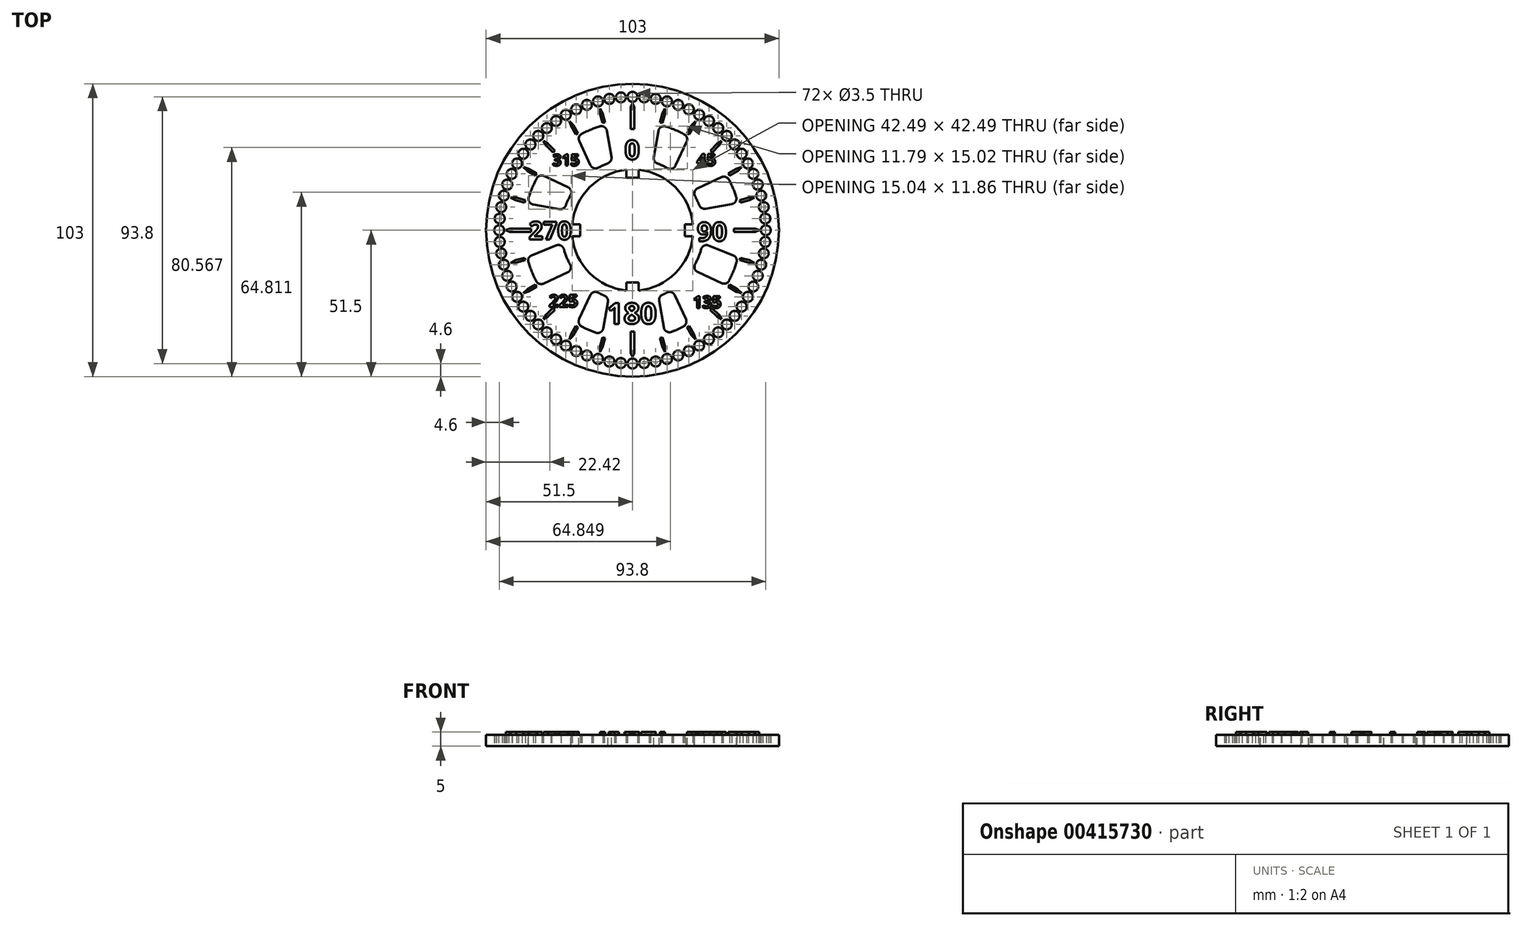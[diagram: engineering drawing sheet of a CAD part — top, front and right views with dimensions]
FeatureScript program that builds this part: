
annotation { "Feature Type Name" : "Feature", "Feature Type Description" : "" }
export const myFeature = defineFeature(function(context is Context, id is Id, definition is map)
    precondition{}
    {
        {
            var Q0;
            Q0=qCreatedBy(makeId("Top.planeOp"),FACE);
            var sketch = newSketch(context, id + "F0", { "sketchPlane" : qUnion([Q0])});
            skArc(sketch, "E0", {"start": v(-2.45, 20.86) * mm, "mid": v(-14.85, 14.85) * mm, "end": v(-20.86, 2.45) * mm});
            skLineSegment(sketch, "E1", {"start": v(0, 35.66) * mm, "end": v(0, -32.33) * mm, "construction": true});
            skLineSegment(sketch, "E2", {"start": v(-36.79, 0) * mm, "end": v(39.43, 0) * mm, "construction": true});
            skCircle(sketch, "E3", {"center": v(0, 0) * mm, "radius": 21.35 * mm});
            skLineSegment(sketch, "E4", {"start": v(0, 18.06) * mm, "end": v(-2.45, 18.06) * mm});
            skLineSegment(sketch, "E5", {"start": v(-2.45, 18.06) * mm, "end": v(-2.45, 20.86) * mm});
            skLineSegment(sketch, "E6.MirrorCS", {"start": v(0, 18.06) * mm, "end": v(2.45, 18.06) * mm});
            skLineSegment(sketch, "E7.MirrorCS", {"start": v(2.45, 18.06) * mm, "end": v(2.45, 20.86) * mm});
            skLineSegment(sketch, "E8.1.0", {"start": v(-18.06, -2.45) * mm, "end": v(-20.86, -2.45) * mm});
            skLineSegment(sketch, "E8.1.1", {"start": v(-18.06, 0) * mm, "end": v(-18.06, -2.45) * mm});
            skLineSegment(sketch, "E8.1.2", {"start": v(-18.06, 0) * mm, "end": v(-18.06, 2.45) * mm});
            skLineSegment(sketch, "E8.1.3", {"start": v(-18.06, 2.45) * mm, "end": v(-20.86, 2.45) * mm});
            skLineSegment(sketch, "E8.2.0", {"start": v(2.45, -18.06) * mm, "end": v(2.45, -20.86) * mm});
            skLineSegment(sketch, "E8.2.1", {"start": v(0, -18.06) * mm, "end": v(2.45, -18.06) * mm});
            skLineSegment(sketch, "E8.2.2", {"start": v(0, -18.06) * mm, "end": v(-2.45, -18.06) * mm});
            skLineSegment(sketch, "E8.2.3", {"start": v(-2.45, -18.06) * mm, "end": v(-2.45, -20.86) * mm});
            skLineSegment(sketch, "E8.3.0", {"start": v(18.06, 2.45) * mm, "end": v(20.86, 2.45) * mm});
            skLineSegment(sketch, "E8.3.1", {"start": v(18.06, 0) * mm, "end": v(18.06, 2.45) * mm});
            skLineSegment(sketch, "E8.3.2", {"start": v(18.06, 0) * mm, "end": v(18.06, -2.45) * mm});
            skLineSegment(sketch, "E8.3.3", {"start": v(18.06, -2.45) * mm, "end": v(20.86, -2.45) * mm});
            skArc(sketch, "E9.trimOffspring", {"start": v(20.86, 2.45) * mm, "mid": v(14.85, 14.85) * mm, "end": v(2.45, 20.86) * mm});
            skArc(sketch, "E10.trimOffspring", {"start": v(2.45, -20.86) * mm, "mid": v(14.85, -14.85) * mm, "end": v(20.86, -2.45) * mm});
            skArc(sketch, "E11.trimOffspring", {"start": v(-20.86, -2.45) * mm, "mid": v(-14.85, -14.85) * mm, "end": v(-2.45, -20.86) * mm});
            skCircle(sketch, "E12", {"center": v(0, 0) * mm, "radius": 24.63 * mm});
            skLineSegment(sketch, "E13", {"start": v(-1.6, 24.58) * mm, "end": v(-1.6, 48.9) * mm});
            skLineSegment(sketch, "E14", {"start": v(-1.6, 48.9) * mm, "end": v(1.67, 48.9) * mm});
            skLineSegment(sketch, "E15", {"start": v(1.67, 48.9) * mm, "end": v(1.67, 24.58) * mm});
            skCircle(sketch, "E16", {"center": v(0, 0) * mm, "radius": 21 * mm, "construction": true});
            skPoint(sketch, "E17", {"position": v(0, 21) * mm});
            skLineSegment(sketch, "E18", {"start": v(-7.13, 21) * mm, "end": v(7.07, 21) * mm, "construction": true});
            skPoint(sketch, "E19", {"position": v(0, 46.9) * mm});
            skLineSegment(sketch, "E20", {"start": v(-18.06, 46.9) * mm, "end": v(18.78, 46.9) * mm, "construction": true});
            skCircle(sketch, "E21", {"center": v(0, 46.9) * mm, "radius": 1.75 * mm});
            skLineSegment(sketch, "E22", {"start": v(-2.1, 21.25) * mm, "end": v(-2.1, 18.4) * mm});
            skLineSegment(sketch, "E23", {"start": v(-2.1, 18.4) * mm, "end": v(2.1, 18.4) * mm});
            skLineSegment(sketch, "E24", {"start": v(2.1, 18.4) * mm, "end": v(2.1, 21.25) * mm});
            skLineSegment(sketch, "E25.1.0", {"start": v(-21.25, -2.1) * mm, "end": v(-18.4, -2.1) * mm});
            skLineSegment(sketch, "E25.1.1", {"start": v(-18.4, -2.1) * mm, "end": v(-18.4, 2.1) * mm});
            skLineSegment(sketch, "E25.1.2", {"start": v(-18.4, 2.1) * mm, "end": v(-21.25, 2.1) * mm});
            skLineSegment(sketch, "E25.2.0", {"start": v(2.1, -21.25) * mm, "end": v(2.1, -18.4) * mm});
            skLineSegment(sketch, "E25.2.1", {"start": v(2.1, -18.4) * mm, "end": v(-2.1, -18.4) * mm});
            skLineSegment(sketch, "E25.2.2", {"start": v(-2.1, -18.4) * mm, "end": v(-2.1, -21.25) * mm});
            skLineSegment(sketch, "E25.3.0", {"start": v(21.25, 2.1) * mm, "end": v(18.4, 2.1) * mm});
            skLineSegment(sketch, "E25.3.1", {"start": v(18.4, 2.1) * mm, "end": v(18.4, -2.1) * mm});
            skLineSegment(sketch, "E25.3.2", {"start": v(18.4, -2.1) * mm, "end": v(21.25, -2.1) * mm});
            skCircle(sketch, "E26", {"center": v(0, 46.9) * mm, "radius": 4.35 * mm});
            skCircle(sketch, "E27", {"center": v(0, 0) * mm, "radius": 51.5 * mm});
            skCircle(sketch, "E28.1.0", {"center": v(-4.09, 46.72) * mm, "radius": 1.75 * mm});
            skCircle(sketch, "E28.2.0", {"center": v(-8.14, 46.19) * mm, "radius": 1.75 * mm});
            skCircle(sketch, "E28.3.0", {"center": v(-12.14, 45.3) * mm, "radius": 1.75 * mm});
            skCircle(sketch, "E28.4.0", {"center": v(-16.04, 44.07) * mm, "radius": 1.75 * mm});
            skCircle(sketch, "E28.5.0", {"center": v(-19.82, 42.5) * mm, "radius": 1.75 * mm});
            skCircle(sketch, "E28.6.0", {"center": v(-23.45, 40.62) * mm, "radius": 1.75 * mm});
            skCircle(sketch, "E28.7.0", {"center": v(-26.9, 38.42) * mm, "radius": 1.75 * mm});
            skCircle(sketch, "E28.8.0", {"center": v(-30.15, 35.93) * mm, "radius": 1.75 * mm});
            skCircle(sketch, "E28.9.0", {"center": v(-33.16, 33.16) * mm, "radius": 1.75 * mm});
            skCircle(sketch, "E28.10.0", {"center": v(-35.93, 30.15) * mm, "radius": 1.75 * mm});
            skCircle(sketch, "E28.11.0", {"center": v(-38.42, 26.9) * mm, "radius": 1.75 * mm});
            skCircle(sketch, "E28.12.0", {"center": v(-40.62, 23.45) * mm, "radius": 1.75 * mm});
            skCircle(sketch, "E28.13.0", {"center": v(-42.5, 19.82) * mm, "radius": 1.75 * mm});
            skCircle(sketch, "E28.14.0", {"center": v(-44.07, 16.04) * mm, "radius": 1.75 * mm});
            skCircle(sketch, "E28.15.0", {"center": v(-45.3, 12.14) * mm, "radius": 1.75 * mm});
            skCircle(sketch, "E28.16.0", {"center": v(-46.19, 8.14) * mm, "radius": 1.75 * mm});
            skCircle(sketch, "E28.17.0", {"center": v(-46.72, 4.09) * mm, "radius": 1.75 * mm});
            skCircle(sketch, "E28.18.0", {"center": v(-46.9, 0) * mm, "radius": 1.75 * mm});
            skCircle(sketch, "E28.19.0", {"center": v(-46.72, -4.09) * mm, "radius": 1.75 * mm});
            skCircle(sketch, "E28.20.0", {"center": v(-46.19, -8.14) * mm, "radius": 1.75 * mm});
            skCircle(sketch, "E28.21.0", {"center": v(-45.3, -12.14) * mm, "radius": 1.75 * mm});
            skCircle(sketch, "E28.22.0", {"center": v(-44.07, -16.04) * mm, "radius": 1.75 * mm});
            skCircle(sketch, "E28.23.0", {"center": v(-42.5, -19.82) * mm, "radius": 1.75 * mm});
            skCircle(sketch, "E28.24.0", {"center": v(-40.62, -23.45) * mm, "radius": 1.75 * mm});
            skCircle(sketch, "E28.25.0", {"center": v(-38.42, -26.9) * mm, "radius": 1.75 * mm});
            skCircle(sketch, "E28.26.0", {"center": v(-35.93, -30.15) * mm, "radius": 1.75 * mm});
            skCircle(sketch, "E28.27.0", {"center": v(-33.16, -33.16) * mm, "radius": 1.75 * mm});
            skCircle(sketch, "E28.28.0", {"center": v(-30.15, -35.93) * mm, "radius": 1.75 * mm});
            skCircle(sketch, "E28.29.0", {"center": v(-26.9, -38.42) * mm, "radius": 1.75 * mm});
            skCircle(sketch, "E28.30.0", {"center": v(-23.45, -40.62) * mm, "radius": 1.75 * mm});
            skCircle(sketch, "E28.31.0", {"center": v(-19.82, -42.5) * mm, "radius": 1.75 * mm});
            skCircle(sketch, "E28.32.0", {"center": v(-16.04, -44.07) * mm, "radius": 1.75 * mm});
            skCircle(sketch, "E28.33.0", {"center": v(-12.14, -45.3) * mm, "radius": 1.75 * mm});
            skCircle(sketch, "E28.34.0", {"center": v(-8.14, -46.19) * mm, "radius": 1.75 * mm});
            skCircle(sketch, "E28.35.0", {"center": v(-4.09, -46.72) * mm, "radius": 1.75 * mm});
            skCircle(sketch, "E28.36.0", {"center": v(0, -46.9) * mm, "radius": 1.75 * mm});
            skCircle(sketch, "E28.37.0", {"center": v(4.09, -46.72) * mm, "radius": 1.75 * mm});
            skCircle(sketch, "E28.38.0", {"center": v(8.14, -46.19) * mm, "radius": 1.75 * mm});
            skCircle(sketch, "E28.39.0", {"center": v(12.14, -45.3) * mm, "radius": 1.75 * mm});
            skCircle(sketch, "E28.40.0", {"center": v(16.04, -44.07) * mm, "radius": 1.75 * mm});
            skCircle(sketch, "E28.41.0", {"center": v(19.82, -42.5) * mm, "radius": 1.75 * mm});
            skCircle(sketch, "E28.42.0", {"center": v(23.45, -40.62) * mm, "radius": 1.75 * mm});
            skCircle(sketch, "E28.43.0", {"center": v(26.9, -38.42) * mm, "radius": 1.75 * mm});
            skCircle(sketch, "E28.44.0", {"center": v(30.15, -35.93) * mm, "radius": 1.75 * mm});
            skCircle(sketch, "E28.45.0", {"center": v(33.16, -33.16) * mm, "radius": 1.75 * mm});
            skCircle(sketch, "E28.46.0", {"center": v(35.93, -30.15) * mm, "radius": 1.75 * mm});
            skCircle(sketch, "E28.47.0", {"center": v(38.42, -26.9) * mm, "radius": 1.75 * mm});
            skCircle(sketch, "E28.48.0", {"center": v(40.62, -23.45) * mm, "radius": 1.75 * mm});
            skCircle(sketch, "E28.49.0", {"center": v(42.5, -19.82) * mm, "radius": 1.75 * mm});
            skCircle(sketch, "E28.50.0", {"center": v(44.07, -16.04) * mm, "radius": 1.75 * mm});
            skCircle(sketch, "E28.51.0", {"center": v(45.3, -12.14) * mm, "radius": 1.75 * mm});
            skCircle(sketch, "E28.52.0", {"center": v(46.19, -8.14) * mm, "radius": 1.75 * mm});
            skCircle(sketch, "E28.53.0", {"center": v(46.72, -4.09) * mm, "radius": 1.75 * mm});
            skCircle(sketch, "E28.54.0", {"center": v(46.9, 0) * mm, "radius": 1.75 * mm});
            skCircle(sketch, "E28.55.0", {"center": v(46.72, 4.09) * mm, "radius": 1.75 * mm});
            skCircle(sketch, "E28.56.0", {"center": v(46.19, 8.14) * mm, "radius": 1.75 * mm});
            skCircle(sketch, "E28.57.0", {"center": v(45.3, 12.14) * mm, "radius": 1.75 * mm});
            skCircle(sketch, "E28.58.0", {"center": v(44.07, 16.04) * mm, "radius": 1.75 * mm});
            skCircle(sketch, "E28.59.0", {"center": v(42.5, 19.82) * mm, "radius": 1.75 * mm});
            skCircle(sketch, "E28.60.0", {"center": v(40.62, 23.45) * mm, "radius": 1.75 * mm});
            skCircle(sketch, "E28.61.0", {"center": v(38.42, 26.9) * mm, "radius": 1.75 * mm});
            skCircle(sketch, "E28.62.0", {"center": v(35.93, 30.15) * mm, "radius": 1.75 * mm});
            skCircle(sketch, "E28.63.0", {"center": v(33.16, 33.16) * mm, "radius": 1.75 * mm});
            skCircle(sketch, "E28.64.0", {"center": v(30.15, 35.93) * mm, "radius": 1.75 * mm});
            skCircle(sketch, "E28.65.0", {"center": v(26.9, 38.42) * mm, "radius": 1.75 * mm});
            skCircle(sketch, "E28.66.0", {"center": v(23.45, 40.62) * mm, "radius": 1.75 * mm});
            skCircle(sketch, "E28.67.0", {"center": v(19.82, 42.5) * mm, "radius": 1.75 * mm});
            skCircle(sketch, "E28.68.0", {"center": v(16.04, 44.07) * mm, "radius": 1.75 * mm});
            skCircle(sketch, "E28.69.0", {"center": v(12.14, 45.3) * mm, "radius": 1.75 * mm});
            skCircle(sketch, "E28.70.0", {"center": v(8.14, 46.19) * mm, "radius": 1.75 * mm});
            skCircle(sketch, "E28.71.0", {"center": v(4.09, 46.72) * mm, "radius": 1.75 * mm});
            skCircle(sketch, "E29", {"center": v(0, 0) * mm, "radius": 42.33 * mm});
            skCircle(sketch, "E30", {"center": v(0, 0) * mm, "radius": 27.68 * mm});
            skSolve(sketch);
        }
        {
            var Q0;
            Q0=makeQuery(id+"F0.imprint","IMPRINT",FACE,{"disambiguationData":[TD([[makeQuery(id+"F0.imprint","IMPRINT",EDGE,{"derivedFrom":sQuery(id+"F0.wireOp",EDGE,"E27")}),1.0]])]});
            var Q1;
            {var subQ16=sQuery(id+"F0.wireOp",EDGE,"E14");Q1=makeQuery(id+"F0.imprint","IMPRINT",FACE,{"disambiguationData":[TD([[makeQuery(id+"F0.imprint","IMPRINT",EDGE,{"derivedFrom":subQ16}),1.0]])]});}
            var Q2;
            {var subQ0=sQuery(id+"F0.wireOp",EDGE,"E26");var subQ1=sQuery(id+"F0.wireOp",EDGE,"E13");var subQ2=makeQuery(id+"F0.imprint","INTERSECT",VERTEX,{"derivedFrom":[subQ1,subQ0]});Q2=makeQuery(id+"F0.imprint","IMPRINT",FACE,{"disambiguationData":[TD([[makeQuery(id+"F0.imprint","IMPRINT",EDGE,{"disambiguationData":[TD([[subQ2,-1.0]])],"derivedFrom":subQ1}),-1.0]])]});}
            var Q3;
            {var subQ0=sQuery(id+"F0.wireOp",EDGE,"E14");Q3=makeQuery(id+"F0.imprint","IMPRINT",FACE,{"disambiguationData":[TD([[makeQuery(id+"F0.imprint","IMPRINT",EDGE,{"derivedFrom":subQ0}),-1.0]])]});}
            var Q4;
            {var subQ0=sQuery(id+"F0.wireOp",EDGE,"E13");var subQ1=sQuery(id+"F0.wireOp",EDGE,"E12");var subQ2=makeQuery(id+"F0.imprint","INTERSECT",VERTEX,{"derivedFrom":[subQ1,subQ0]});Q4=makeQuery(id+"F0.imprint","IMPRINT",FACE,{"disambiguationData":[TD([[makeQuery(id+"F0.imprint","IMPRINT",EDGE,{"disambiguationData":[TD([[subQ2,1.0]])],"derivedFrom":subQ1}),-1.0]])]});}
            var Q5;
            {var subQ0=sQuery(id+"F0.wireOp",EDGE,"E3");var subQ4=makeQuery(id+"F0.imprint","INTERSECT",VERTEX,{"derivedFrom":[subQ0,sQuery(id+"F0.wireOp",EDGE,"E24")]});Q5=makeQuery(id+"F0.imprint","IMPRINT",FACE,{"disambiguationData":[TD([[makeQuery(id+"F0.imprint","IMPRINT",EDGE,{"disambiguationData":[TD([[subQ4,1.0]])],"derivedFrom":subQ0}),-1.0]])]});}
            var Q6;
            {var subQ5=sQuery(id+"F0.wireOp",EDGE,"E25.1.1");Q6=makeQuery(id+"F0.imprint","IMPRINT",FACE,{"disambiguationData":[TD([[makeQuery(id+"F0.imprint","IMPRINT",EDGE,{"derivedFrom":subQ5}),1.0]])]});}
            var Q7;
            {var subQ0=sQuery(id+"F0.wireOp",EDGE,"E22");Q7=makeQuery(id+"F0.imprint","IMPRINT",FACE,{"disambiguationData":[TD([[makeQuery(id+"F0.imprint","IMPRINT",EDGE,{"derivedFrom":subQ0}),1.0]])]});}
            var Q8;
            {var subQ5=sQuery(id+"F0.wireOp",EDGE,"E25.3.1");Q8=makeQuery(id+"F0.imprint","IMPRINT",FACE,{"disambiguationData":[TD([[makeQuery(id+"F0.imprint","IMPRINT",EDGE,{"derivedFrom":subQ5}),1.0]])]});}
            var Q9;
            {var subQ5=sQuery(id+"F0.wireOp",EDGE,"E25.2.1");Q9=makeQuery(id+"F0.imprint","IMPRINT",FACE,{"disambiguationData":[TD([[makeQuery(id+"F0.imprint","IMPRINT",EDGE,{"derivedFrom":subQ5}),1.0]])]});}
            var Q10;
            {var subQ0=sQuery(id+"F0.wireOp",EDGE,"E30");var subQ1=sQuery(id+"F0.wireOp",EDGE,"E13");var subQ2=makeQuery(id+"F0.imprint","INTERSECT",VERTEX,{"derivedFrom":[subQ1,subQ0]});Q10=makeQuery(id+"F0.imprint","IMPRINT",FACE,{"disambiguationData":[TD([[makeQuery(id+"F0.imprint","IMPRINT",EDGE,{"disambiguationData":[TD([[subQ2,-1.0]])],"derivedFrom":subQ1}),1.0]])]});}
            var Q11;
            {var subQ0=sQuery(id+"F0.wireOp",EDGE,"E13");var subQ1=sQuery(id+"F0.wireOp",EDGE,"E12");var subQ2=makeQuery(id+"F0.imprint","INTERSECT",VERTEX,{"derivedFrom":[subQ1,subQ0]});Q11=makeQuery(id+"F0.imprint","IMPRINT",FACE,{"disambiguationData":[TD([[makeQuery(id+"F0.imprint","IMPRINT",EDGE,{"disambiguationData":[TD([[subQ2,-1.0]])],"derivedFrom":subQ1}),-1.0]])]});}
            var Q12;
            {var subQ0=sQuery(id+"F0.wireOp",EDGE,"E30");var subQ1=sQuery(id+"F0.wireOp",EDGE,"E13");var subQ2=makeQuery(id+"F0.imprint","INTERSECT",VERTEX,{"derivedFrom":[subQ1,subQ0]});Q12=makeQuery(id+"F0.imprint","IMPRINT",FACE,{"disambiguationData":[TD([[makeQuery(id+"F0.imprint","IMPRINT",EDGE,{"disambiguationData":[TD([[subQ2,-1.0]])],"derivedFrom":subQ1}),-1.0]])]});}
            var Q13;
            {var subQ0=sQuery(id+"F0.wireOp",EDGE,"E29");var subQ1=sQuery(id+"F0.wireOp",EDGE,"E13");var subQ2=makeQuery(id+"F0.imprint","INTERSECT",VERTEX,{"derivedFrom":[subQ1,subQ0]});Q13=makeQuery(id+"F0.imprint","IMPRINT",FACE,{"disambiguationData":[TD([[makeQuery(id+"F0.imprint","IMPRINT",EDGE,{"disambiguationData":[TD([[subQ2,-1.0]])],"derivedFrom":subQ1}),-1.0]])]});}
            extrude(context, id + "F1", {"entities" : qUnion([Q0, Q1, Q2, Q3, Q4, Q5, Q6, Q7, Q8, Q9, Q10, Q11, Q12, Q13]), "depth" : 4 * mm});
        }
        {
            var Q0;
            Q0=makeQuery(id+"F1.opExtrude","CAP_FACE",FACE,{"disambiguationData":[OSD([sQuery(id+"F0.wireOp",EDGE,"E3"),sQuery(id+"F0.wireOp",EDGE,"E21"),sQuery(id+"F0.wireOp",EDGE,"E22"),sQuery(id+"F0.wireOp",EDGE,"E23"),sQuery(id+"F0.wireOp",EDGE,"E24"),sQuery(id+"F0.wireOp",EDGE,"E25.1.0"),sQuery(id+"F0.wireOp",EDGE,"E25.1.1"),sQuery(id+"F0.wireOp",EDGE,"E25.1.2"),sQuery(id+"F0.wireOp",EDGE,"E25.2.0"),sQuery(id+"F0.wireOp",EDGE,"E25.2.1"),sQuery(id+"F0.wireOp",EDGE,"E25.2.2"),sQuery(id+"F0.wireOp",EDGE,"E25.3.0"),sQuery(id+"F0.wireOp",EDGE,"E25.3.1"),sQuery(id+"F0.wireOp",EDGE,"E25.3.2"),sQuery(id+"F0.wireOp",EDGE,"E27"),sQuery(id+"F0.wireOp",EDGE,"E28.1.0"),sQuery(id+"F0.wireOp",EDGE,"E28.2.0"),sQuery(id+"F0.wireOp",EDGE,"E28.3.0"),sQuery(id+"F0.wireOp",EDGE,"E28.4.0"),sQuery(id+"F0.wireOp",EDGE,"E28.5.0"),sQuery(id+"F0.wireOp",EDGE,"E28.6.0"),sQuery(id+"F0.wireOp",EDGE,"E28.7.0"),sQuery(id+"F0.wireOp",EDGE,"E28.8.0"),sQuery(id+"F0.wireOp",EDGE,"E28.9.0"),sQuery(id+"F0.wireOp",EDGE,"E28.10.0"),sQuery(id+"F0.wireOp",EDGE,"E28.11.0"),sQuery(id+"F0.wireOp",EDGE,"E28.12.0"),sQuery(id+"F0.wireOp",EDGE,"E28.13.0"),sQuery(id+"F0.wireOp",EDGE,"E28.14.0"),sQuery(id+"F0.wireOp",EDGE,"E28.15.0"),sQuery(id+"F0.wireOp",EDGE,"E28.16.0"),sQuery(id+"F0.wireOp",EDGE,"E28.17.0"),sQuery(id+"F0.wireOp",EDGE,"E28.18.0"),sQuery(id+"F0.wireOp",EDGE,"E28.19.0"),sQuery(id+"F0.wireOp",EDGE,"E28.20.0"),sQuery(id+"F0.wireOp",EDGE,"E28.21.0"),sQuery(id+"F0.wireOp",EDGE,"E28.22.0"),sQuery(id+"F0.wireOp",EDGE,"E28.23.0"),sQuery(id+"F0.wireOp",EDGE,"E28.24.0"),sQuery(id+"F0.wireOp",EDGE,"E28.25.0"),sQuery(id+"F0.wireOp",EDGE,"E28.26.0"),sQuery(id+"F0.wireOp",EDGE,"E28.27.0"),sQuery(id+"F0.wireOp",EDGE,"E28.28.0"),sQuery(id+"F0.wireOp",EDGE,"E28.29.0"),sQuery(id+"F0.wireOp",EDGE,"E28.30.0"),sQuery(id+"F0.wireOp",EDGE,"E28.31.0"),sQuery(id+"F0.wireOp",EDGE,"E28.32.0"),sQuery(id+"F0.wireOp",EDGE,"E28.33.0"),sQuery(id+"F0.wireOp",EDGE,"E28.34.0"),sQuery(id+"F0.wireOp",EDGE,"E28.35.0"),sQuery(id+"F0.wireOp",EDGE,"E28.36.0"),sQuery(id+"F0.wireOp",EDGE,"E28.37.0"),sQuery(id+"F0.wireOp",EDGE,"E28.38.0"),sQuery(id+"F0.wireOp",EDGE,"E28.39.0"),sQuery(id+"F0.wireOp",EDGE,"E28.40.0"),sQuery(id+"F0.wireOp",EDGE,"E28.41.0"),sQuery(id+"F0.wireOp",EDGE,"E28.42.0"),sQuery(id+"F0.wireOp",EDGE,"E28.43.0"),sQuery(id+"F0.wireOp",EDGE,"E28.44.0"),sQuery(id+"F0.wireOp",EDGE,"E28.45.0"),sQuery(id+"F0.wireOp",EDGE,"E28.46.0"),sQuery(id+"F0.wireOp",EDGE,"E28.47.0"),sQuery(id+"F0.wireOp",EDGE,"E28.48.0"),sQuery(id+"F0.wireOp",EDGE,"E28.49.0"),sQuery(id+"F0.wireOp",EDGE,"E28.50.0"),sQuery(id+"F0.wireOp",EDGE,"E28.51.0"),sQuery(id+"F0.wireOp",EDGE,"E28.52.0"),sQuery(id+"F0.wireOp",EDGE,"E28.53.0"),sQuery(id+"F0.wireOp",EDGE,"E28.54.0"),sQuery(id+"F0.wireOp",EDGE,"E28.55.0"),sQuery(id+"F0.wireOp",EDGE,"E28.56.0"),sQuery(id+"F0.wireOp",EDGE,"E28.57.0"),sQuery(id+"F0.wireOp",EDGE,"E28.58.0"),sQuery(id+"F0.wireOp",EDGE,"E28.59.0"),sQuery(id+"F0.wireOp",EDGE,"E28.60.0"),sQuery(id+"F0.wireOp",EDGE,"E28.61.0"),sQuery(id+"F0.wireOp",EDGE,"E28.62.0"),sQuery(id+"F0.wireOp",EDGE,"E28.63.0"),sQuery(id+"F0.wireOp",EDGE,"E28.64.0"),sQuery(id+"F0.wireOp",EDGE,"E28.65.0"),sQuery(id+"F0.wireOp",EDGE,"E28.66.0"),sQuery(id+"F0.wireOp",EDGE,"E28.67.0"),sQuery(id+"F0.wireOp",EDGE,"E28.68.0"),sQuery(id+"F0.wireOp",EDGE,"E28.69.0"),sQuery(id+"F0.wireOp",EDGE,"E28.70.0"),sQuery(id+"F0.wireOp",EDGE,"E28.71.0")])],"isStart":false});
            var sketch = newSketch(context, id + "F2", { "sketchPlane" : qUnion([Q0])});
            skCircle(sketch, "E31", {"center": v(0, 0) * mm, "radius": 42.4 * mm});
            skCircle(sketch, "E32", {"center": v(0, 0) * mm, "radius": 25.92 * mm});
            skSolve(sketch);
        }
        {
            var Q0;
            Q0=makeQuery(id+"F1.opExtrude","CAP_FACE",FACE,{"disambiguationData":[OSD([sQuery(id+"F0.wireOp",EDGE,"E3"),sQuery(id+"F0.wireOp",EDGE,"E21"),sQuery(id+"F0.wireOp",EDGE,"E22"),sQuery(id+"F0.wireOp",EDGE,"E23"),sQuery(id+"F0.wireOp",EDGE,"E24"),sQuery(id+"F0.wireOp",EDGE,"E25.1.0"),sQuery(id+"F0.wireOp",EDGE,"E25.1.1"),sQuery(id+"F0.wireOp",EDGE,"E25.1.2"),sQuery(id+"F0.wireOp",EDGE,"E25.2.0"),sQuery(id+"F0.wireOp",EDGE,"E25.2.1"),sQuery(id+"F0.wireOp",EDGE,"E25.2.2"),sQuery(id+"F0.wireOp",EDGE,"E25.3.0"),sQuery(id+"F0.wireOp",EDGE,"E25.3.1"),sQuery(id+"F0.wireOp",EDGE,"E25.3.2"),sQuery(id+"F0.wireOp",EDGE,"E27"),sQuery(id+"F0.wireOp",EDGE,"E28.1.0"),sQuery(id+"F0.wireOp",EDGE,"E28.2.0"),sQuery(id+"F0.wireOp",EDGE,"E28.3.0"),sQuery(id+"F0.wireOp",EDGE,"E28.4.0"),sQuery(id+"F0.wireOp",EDGE,"E28.5.0"),sQuery(id+"F0.wireOp",EDGE,"E28.6.0"),sQuery(id+"F0.wireOp",EDGE,"E28.7.0"),sQuery(id+"F0.wireOp",EDGE,"E28.8.0"),sQuery(id+"F0.wireOp",EDGE,"E28.9.0"),sQuery(id+"F0.wireOp",EDGE,"E28.10.0"),sQuery(id+"F0.wireOp",EDGE,"E28.11.0"),sQuery(id+"F0.wireOp",EDGE,"E28.12.0"),sQuery(id+"F0.wireOp",EDGE,"E28.13.0"),sQuery(id+"F0.wireOp",EDGE,"E28.14.0"),sQuery(id+"F0.wireOp",EDGE,"E28.15.0"),sQuery(id+"F0.wireOp",EDGE,"E28.16.0"),sQuery(id+"F0.wireOp",EDGE,"E28.17.0"),sQuery(id+"F0.wireOp",EDGE,"E28.18.0"),sQuery(id+"F0.wireOp",EDGE,"E28.19.0"),sQuery(id+"F0.wireOp",EDGE,"E28.20.0"),sQuery(id+"F0.wireOp",EDGE,"E28.21.0"),sQuery(id+"F0.wireOp",EDGE,"E28.22.0"),sQuery(id+"F0.wireOp",EDGE,"E28.23.0"),sQuery(id+"F0.wireOp",EDGE,"E28.24.0"),sQuery(id+"F0.wireOp",EDGE,"E28.25.0"),sQuery(id+"F0.wireOp",EDGE,"E28.26.0"),sQuery(id+"F0.wireOp",EDGE,"E28.27.0"),sQuery(id+"F0.wireOp",EDGE,"E28.28.0"),sQuery(id+"F0.wireOp",EDGE,"E28.29.0"),sQuery(id+"F0.wireOp",EDGE,"E28.30.0"),sQuery(id+"F0.wireOp",EDGE,"E28.31.0"),sQuery(id+"F0.wireOp",EDGE,"E28.32.0"),sQuery(id+"F0.wireOp",EDGE,"E28.33.0"),sQuery(id+"F0.wireOp",EDGE,"E28.34.0"),sQuery(id+"F0.wireOp",EDGE,"E28.35.0"),sQuery(id+"F0.wireOp",EDGE,"E28.36.0"),sQuery(id+"F0.wireOp",EDGE,"E28.37.0"),sQuery(id+"F0.wireOp",EDGE,"E28.38.0"),sQuery(id+"F0.wireOp",EDGE,"E28.39.0"),sQuery(id+"F0.wireOp",EDGE,"E28.40.0"),sQuery(id+"F0.wireOp",EDGE,"E28.41.0"),sQuery(id+"F0.wireOp",EDGE,"E28.42.0"),sQuery(id+"F0.wireOp",EDGE,"E28.43.0"),sQuery(id+"F0.wireOp",EDGE,"E28.44.0"),sQuery(id+"F0.wireOp",EDGE,"E28.45.0"),sQuery(id+"F0.wireOp",EDGE,"E28.46.0"),sQuery(id+"F0.wireOp",EDGE,"E28.47.0"),sQuery(id+"F0.wireOp",EDGE,"E28.48.0"),sQuery(id+"F0.wireOp",EDGE,"E28.49.0"),sQuery(id+"F0.wireOp",EDGE,"E28.50.0"),sQuery(id+"F0.wireOp",EDGE,"E28.51.0"),sQuery(id+"F0.wireOp",EDGE,"E28.52.0"),sQuery(id+"F0.wireOp",EDGE,"E28.53.0"),sQuery(id+"F0.wireOp",EDGE,"E28.54.0"),sQuery(id+"F0.wireOp",EDGE,"E28.55.0"),sQuery(id+"F0.wireOp",EDGE,"E28.56.0"),sQuery(id+"F0.wireOp",EDGE,"E28.57.0"),sQuery(id+"F0.wireOp",EDGE,"E28.58.0"),sQuery(id+"F0.wireOp",EDGE,"E28.59.0"),sQuery(id+"F0.wireOp",EDGE,"E28.60.0"),sQuery(id+"F0.wireOp",EDGE,"E28.61.0"),sQuery(id+"F0.wireOp",EDGE,"E28.62.0"),sQuery(id+"F0.wireOp",EDGE,"E28.63.0"),sQuery(id+"F0.wireOp",EDGE,"E28.64.0"),sQuery(id+"F0.wireOp",EDGE,"E28.65.0"),sQuery(id+"F0.wireOp",EDGE,"E28.66.0"),sQuery(id+"F0.wireOp",EDGE,"E28.67.0"),sQuery(id+"F0.wireOp",EDGE,"E28.68.0"),sQuery(id+"F0.wireOp",EDGE,"E28.69.0"),sQuery(id+"F0.wireOp",EDGE,"E28.70.0"),sQuery(id+"F0.wireOp",EDGE,"E28.71.0")])],"isStart":false});
            var sketch = newSketch(context, id + "F3", { "sketchPlane" : qUnion([Q0])});
            skLineSegment(sketch, "E33", {"start": v(0, 43.22) * mm, "end": v(-0.58, 43.22) * mm});
            skLineSegment(sketch, "E34", {"start": v(-0.58, 43.22) * mm, "end": v(-0.58, 35.64) * mm});
            skLineSegment(sketch, "E35", {"start": v(-0.58, 35.64) * mm, "end": v(0, 35.64) * mm});
            skLineSegment(sketch, "E36", {"start": v(0, 44.58) * mm, "end": v(0, 29) * mm, "construction": true});
            skLineSegment(sketch, "E37.MirrorCS", {"start": v(0, 43.22) * mm, "end": v(0.58, 43.22) * mm});
            skLineSegment(sketch, "E38.MirrorCS", {"start": v(0.58, 43.22) * mm, "end": v(0.58, 35.64) * mm});
            skLineSegment(sketch, "E39.MirrorCS", {"start": v(0.58, 35.64) * mm, "end": v(0, 35.64) * mm});
            skLineSegment(sketch, "E40", {"start": v(-0.58, 43.22) * mm, "end": v(0, 44.58) * mm});
            skLineSegment(sketch, "E41", {"start": v(0.58, 43.22) * mm, "end": v(0, 44.58) * mm});
            skText(sketch, "E42", { "text": "0", "fontName": "OpenSans-Bold.ttf"});
            skLineSegment(sketch, "E43.1.0", {"start": v(-43.22, -0.58) * mm, "end": v(-44.58, 0) * mm});
            skLineSegment(sketch, "E43.1.1", {"start": v(-43.22, 0.58) * mm, "end": v(-44.58, 0) * mm});
            skLineSegment(sketch, "E43.1.2", {"start": v(-43.22, 0.58) * mm, "end": v(-35.64, 0.58) * mm});
            skLineSegment(sketch, "E43.1.3", {"start": v(-35.64, 0.58) * mm, "end": v(-35.64, 0) * mm});
            skLineSegment(sketch, "E43.1.4", {"start": v(-35.64, -0.58) * mm, "end": v(-35.64, 0) * mm});
            skLineSegment(sketch, "E43.1.5", {"start": v(-43.22, -0.58) * mm, "end": v(-35.64, -0.58) * mm});
            skLineSegment(sketch, "E43.2.0", {"start": v(0.58, -43.22) * mm, "end": v(0, -44.58) * mm});
            skLineSegment(sketch, "E43.2.1", {"start": v(-0.58, -43.22) * mm, "end": v(0, -44.58) * mm});
            skLineSegment(sketch, "E43.2.2", {"start": v(-0.58, -43.22) * mm, "end": v(-0.58, -35.64) * mm});
            skLineSegment(sketch, "E43.2.3", {"start": v(-0.58, -35.64) * mm, "end": v(0, -35.64) * mm});
            skLineSegment(sketch, "E43.2.4", {"start": v(0.58, -35.64) * mm, "end": v(0, -35.64) * mm});
            skLineSegment(sketch, "E43.2.5", {"start": v(0.58, -43.22) * mm, "end": v(0.58, -35.64) * mm});
            skLineSegment(sketch, "E43.3.0", {"start": v(43.22, 0.58) * mm, "end": v(44.58, 0) * mm});
            skLineSegment(sketch, "E43.3.1", {"start": v(43.22, -0.58) * mm, "end": v(44.58, 0) * mm});
            skLineSegment(sketch, "E43.3.2", {"start": v(43.22, -0.58) * mm, "end": v(35.64, -0.58) * mm});
            skLineSegment(sketch, "E43.3.3", {"start": v(35.64, -0.58) * mm, "end": v(35.64, 0) * mm});
            skLineSegment(sketch, "E43.3.4", {"start": v(35.64, 0.58) * mm, "end": v(35.64, 0) * mm});
            skLineSegment(sketch, "E43.3.5", {"start": v(43.22, 0.58) * mm, "end": v(35.64, 0.58) * mm});
            skPoint(sketch, "E43.center", {"position": v(0, 0) * mm});
            skText(sketch, "E44", { "text": "90", "fontName": "OpenSans-Bold.ttf"});
            skText(sketch, "E45", { "text": "180", "fontName": "OpenSans-Bold.ttf"});
            skPoint(sketch, "E46", {"position": v(0, 36.8) * mm});
            skText(sketch, "E47", { "text": "270", "fontName": "OpenSans-Bold.ttf"});
            const initialGuessF3  = {"E42": [-0.00281, 0.02492, 1, 0, 0.00675], "E44": [0.0227, -0.0038, 1, 0, 0.00662], "E45": [-0.00899, -0.03293, 1, 0, 0.00736], "E47": [-0.03652, -0.00328, 1, 0, 0.00634]};
            skSetInitialGuess(sketch, initialGuessF3);
            skSolve(sketch);
        }
        {
            var Q0;
            Q0 = qSketchRegion(id + "F3", true);
            extrude(context, id + "F4", {"entities" : qUnion([Q0]), "operationType" : NewBodyOperationType.ADD, "depth" : 1 * mm});
        }
        {
            var Q0;
            {var subQ0=sQuery(id+"F0.wireOp",EDGE,"E28.27.0");var subQ1=sQuery(id+"F0.wireOp",EDGE,"E28.26.0");var subQ2=sQuery(id+"F0.wireOp",EDGE,"E28.25.0");var subQ3=sQuery(id+"F0.wireOp",EDGE,"E28.46.0");var subQ4=sQuery(id+"F0.wireOp",EDGE,"E28.24.0");var subQ5=sQuery(id+"F0.wireOp",EDGE,"E28.45.0");var subQ6=sQuery(id+"F0.wireOp",EDGE,"E28.23.0");var subQ7=sQuery(id+"F0.wireOp",EDGE,"E28.44.0");var subQ8=sQuery(id+"F0.wireOp",EDGE,"E28.22.0");var subQ9=sQuery(id+"F0.wireOp",EDGE,"E28.43.0");var subQ10=sQuery(id+"F0.wireOp",EDGE,"E28.21.0");var subQ11=sQuery(id+"F0.wireOp",EDGE,"E28.42.0");var subQ12=sQuery(id+"F0.wireOp",EDGE,"E28.20.0");var subQ13=sQuery(id+"F0.wireOp",EDGE,"E28.41.0");var subQ14=sQuery(id+"F0.wireOp",EDGE,"E28.19.0");var subQ15=sQuery(id+"F0.wireOp",EDGE,"E28.17.0");var subQ16=sQuery(id+"F0.wireOp",EDGE,"E28.16.0");var subQ17=sQuery(id+"F0.wireOp",EDGE,"E28.10.0");var subQ18=sQuery(id+"F0.wireOp",EDGE,"E28.9.0");var subQ19=sQuery(id+"F0.wireOp",EDGE,"E28.18.0");var subQ20=sQuery(id+"F0.wireOp",EDGE,"E28.40.0");var subQ21=sQuery(id+"F0.wireOp",EDGE,"E28.7.0");var subQ22=sQuery(id+"F0.wireOp",EDGE,"E28.6.0");var subQ23=sQuery(id+"F0.wireOp",EDGE,"E28.15.0");var subQ24=sQuery(id+"F0.wireOp",EDGE,"E28.37.0");var subQ25=sQuery(id+"F0.wireOp",EDGE,"E28.5.0");var subQ26=sQuery(id+"F0.wireOp",EDGE,"E28.14.0");var subQ27=sQuery(id+"F0.wireOp",EDGE,"E28.36.0");var subQ28=sQuery(id+"F0.wireOp",EDGE,"E25.1.0");var subQ29=sQuery(id+"F0.wireOp",EDGE,"E24");var subQ30=sQuery(id+"F0.wireOp",EDGE,"E23");var subQ31=sQuery(id+"F0.wireOp",EDGE,"E22");var subQ32=sQuery(id+"F0.wireOp",EDGE,"E21");var subQ33=sQuery(id+"F0.wireOp",EDGE,"E25.1.1");var subQ34=sQuery(id+"F0.wireOp",EDGE,"E28.28.0");var subQ35=sQuery(id+"F0.wireOp",EDGE,"E3");var subQ36=sQuery(id+"F0.wireOp",EDGE,"E25.3.0");var subQ37=sQuery(id+"F0.wireOp",EDGE,"E28.4.0");var subQ38=sQuery(id+"F0.wireOp",EDGE,"E28.13.0");var subQ39=sQuery(id+"F0.wireOp",EDGE,"E28.35.0");var subQ40=sQuery(id+"F0.wireOp",EDGE,"E25.2.0");var subQ41=sQuery(id+"F0.wireOp",EDGE,"E25.3.2");var subQ42=sQuery(id+"F0.wireOp",EDGE,"E25.1.2");var subQ43=sQuery(id+"F0.wireOp",EDGE,"E25.2.2");var subQ44=sQuery(id+"F0.wireOp",EDGE,"E25.2.1");var subQ45=sQuery(id+"F0.wireOp",EDGE,"E25.3.1");var subQ46=sQuery(id+"F0.wireOp",EDGE,"E28.8.0");var subQ47=sQuery(id+"F0.wireOp",EDGE,"E28.30.0");var subQ48=sQuery(id+"F0.wireOp",EDGE,"E27");var subQ49=sQuery(id+"F0.wireOp",EDGE,"E28.1.0");var subQ50=sQuery(id+"F0.wireOp",EDGE,"E28.2.0");var subQ51=sQuery(id+"F0.wireOp",EDGE,"E28.11.0");var subQ52=sQuery(id+"F0.wireOp",EDGE,"E28.33.0");var subQ53=sQuery(id+"F0.wireOp",EDGE,"E28.3.0");var subQ54=sQuery(id+"F0.wireOp",EDGE,"E28.12.0");var subQ55=sQuery(id+"F0.wireOp",EDGE,"E28.34.0");var subQ56=sQuery(id+"F0.wireOp",EDGE,"E28.29.0");var subQ57=sQuery(id+"F0.wireOp",EDGE,"E28.31.0");var subQ58=sQuery(id+"F0.wireOp",EDGE,"E28.32.0");var subQ59=sQuery(id+"F0.wireOp",EDGE,"E28.55.0");var subQ60=sQuery(id+"F0.wireOp",EDGE,"E28.58.0");var subQ61=sQuery(id+"F0.wireOp",EDGE,"E28.59.0");var subQ62=sQuery(id+"F0.wireOp",EDGE,"E28.60.0");var subQ63=sQuery(id+"F0.wireOp",EDGE,"E28.38.0");var subQ64=sQuery(id+"F0.wireOp",EDGE,"E28.61.0");var subQ65=sQuery(id+"F0.wireOp",EDGE,"E28.39.0");var subQ66=sQuery(id+"F0.wireOp",EDGE,"E28.62.0");var subQ67=sQuery(id+"F0.wireOp",EDGE,"E28.65.0");var subQ68=sQuery(id+"F0.wireOp",EDGE,"E28.66.0");var subQ69=sQuery(id+"F0.wireOp",EDGE,"E28.67.0");var subQ70=sQuery(id+"F0.wireOp",EDGE,"E28.68.0");var subQ71=sQuery(id+"F0.wireOp",EDGE,"E28.69.0");var subQ72=sQuery(id+"F0.wireOp",EDGE,"E28.47.0");var subQ73=sQuery(id+"F0.wireOp",EDGE,"E28.48.0");var subQ74=sQuery(id+"F0.wireOp",EDGE,"E28.49.0");var subQ75=sQuery(id+"F0.wireOp",EDGE,"E28.50.0");var subQ76=sQuery(id+"F0.wireOp",EDGE,"E28.51.0");var subQ77=sQuery(id+"F0.wireOp",EDGE,"E28.52.0");var subQ78=sQuery(id+"F0.wireOp",EDGE,"E28.53.0");var subQ79=sQuery(id+"F0.wireOp",EDGE,"E28.54.0");var subQ80=sQuery(id+"F0.wireOp",EDGE,"E28.56.0");var subQ81=sQuery(id+"F0.wireOp",EDGE,"E28.57.0");var subQ82=sQuery(id+"F0.wireOp",EDGE,"E28.63.0");var subQ83=sQuery(id+"F0.wireOp",EDGE,"E28.64.0");var subQ84=sQuery(id+"F0.wireOp",EDGE,"E28.70.0");var subQ85=sQuery(id+"F0.wireOp",EDGE,"E28.71.0");Q0=makeQuery(id+"F4.boolean.opBoolean","SPLIT",FACE,{"disambiguationData":[TD([makeQuery(id+"F1.opExtrude","SWEPT_FACE",FACE,{"disambiguationData":[OSD([subQ32])]})])],"derivedFrom":makeQuery(id+"F1.opExtrude","CAP_FACE",FACE,{"disambiguationData":[OSD([subQ35,subQ32,subQ31,subQ30,subQ29,subQ28,subQ33,subQ42,subQ40,subQ44,subQ43,subQ36,subQ45,subQ41,subQ48,subQ49,subQ50,subQ53,subQ37,subQ25,subQ22,subQ21,subQ46,subQ18,subQ17,subQ51,subQ54,subQ38,subQ26,subQ23,subQ16,subQ15,subQ19,subQ14,subQ12,subQ10,subQ8,subQ6,subQ4,subQ2,subQ1,subQ0,subQ34,subQ56,subQ47,subQ57,subQ58,subQ52,subQ55,subQ39,subQ27,subQ24,subQ63,subQ65,subQ20,subQ13,subQ11,subQ9,subQ7,subQ5,subQ3,subQ72,subQ73,subQ74,subQ75,subQ76,subQ77,subQ78,subQ79,subQ59,subQ80,subQ81,subQ60,subQ61,subQ62,subQ64,subQ66,subQ82,subQ83,subQ67,subQ68,subQ69,subQ70,subQ71,subQ84,subQ85])],"isStart":false})});}
            var sketch = newSketch(context, id + "F5", { "sketchPlane" : qUnion([Q0])});
            skLineSegment(sketch, "E48", {"start": v(27.37, 27.99) * mm, "end": v(29.73, 30.35) * mm});
            skLineSegment(sketch, "E49", {"start": v(29.73, 30.35) * mm, "end": v(30.36, 29.71) * mm});
            skLineSegment(sketch, "E50", {"start": v(30.36, 29.71) * mm, "end": v(28, 27.35) * mm});
            skLineSegment(sketch, "E51", {"start": v(28, 27.35) * mm, "end": v(27.37, 27.99) * mm});
            skLineSegment(sketch, "E52", {"start": v(-11.67, 0) * mm, "end": v(11.76, 0) * mm, "construction": true});
            skLineSegment(sketch, "E53", {"start": v(0, 14.21) * mm, "end": v(0, -13.47) * mm, "construction": true});
            skLineSegment(sketch, "E54", {"start": v(29.73, 30.35) * mm, "end": v(31.39, 31.39) * mm});
            skLineSegment(sketch, "E55", {"start": v(31.39, 31.39) * mm, "end": v(30.36, 29.71) * mm});
            skPoint(sketch, "E56", {"position": v(33.16, 33.16) * mm});
            skLineSegment(sketch, "E57", {"start": v(33.16, 33.16) * mm, "end": v(0, 0) * mm, "construction": true});
            skText(sketch, "E58", { "text": "45", "fontName": "OpenSans-Bold.ttf"});
            skLineSegment(sketch, "E59.1.0", {"start": v(19.2, 34.12) * mm, "end": v(20.86, 37) * mm});
            skLineSegment(sketch, "E59.1.1", {"start": v(20.86, 37) * mm, "end": v(22.2, 38.44) * mm});
            skLineSegment(sketch, "E59.1.2", {"start": v(22.2, 38.44) * mm, "end": v(21.64, 36.56) * mm});
            skLineSegment(sketch, "E59.1.3", {"start": v(21.64, 36.56) * mm, "end": v(19.97, 33.67) * mm});
            skLineSegment(sketch, "E59.1.4", {"start": v(19.97, 33.67) * mm, "end": v(19.2, 34.12) * mm});
            skLineSegment(sketch, "E59.2.0", {"start": v(9.7, 37.92) * mm, "end": v(10.57, 41.15) * mm});
            skLineSegment(sketch, "E59.2.1", {"start": v(10.57, 41.15) * mm, "end": v(11.49, 42.88) * mm});
            skLineSegment(sketch, "E59.2.2", {"start": v(11.49, 42.88) * mm, "end": v(11.44, 40.91) * mm});
            skLineSegment(sketch, "E59.2.3", {"start": v(11.44, 40.91) * mm, "end": v(10.57, 37.7) * mm});
            skLineSegment(sketch, "E59.2.4", {"start": v(10.57, 37.7) * mm, "end": v(9.7, 37.92) * mm});
            skLineSegment(sketch, "E59.3.0", {"start": v(-0.44, 39.14) * mm, "end": v(-0.44, 42.48) * mm});
            skLineSegment(sketch, "E59.3.1", {"start": v(-0.44, 42.48) * mm, "end": v(0, 44.4) * mm});
            skLineSegment(sketch, "E59.3.2", {"start": v(0, 44.4) * mm, "end": v(0.46, 42.48) * mm});
            skLineSegment(sketch, "E59.3.3", {"start": v(0.46, 42.48) * mm, "end": v(0.46, 39.14) * mm});
            skLineSegment(sketch, "E59.3.4", {"start": v(0.46, 39.14) * mm, "end": v(-0.44, 39.14) * mm});
            skLineSegment(sketch, "E59.4.0", {"start": v(-10.55, 37.7) * mm, "end": v(-11.42, 40.92) * mm});
            skLineSegment(sketch, "E59.4.1", {"start": v(-11.42, 40.92) * mm, "end": v(-11.49, 42.88) * mm});
            skLineSegment(sketch, "E59.4.2", {"start": v(-11.49, 42.88) * mm, "end": v(-10.55, 41.15) * mm});
            skLineSegment(sketch, "E59.4.3", {"start": v(-10.55, 41.15) * mm, "end": v(-9.69, 37.93) * mm});
            skLineSegment(sketch, "E59.4.4", {"start": v(-9.69, 37.93) * mm, "end": v(-10.55, 37.7) * mm});
            skLineSegment(sketch, "E59.5.0", {"start": v(-19.95, 33.68) * mm, "end": v(-21.62, 36.57) * mm});
            skLineSegment(sketch, "E59.5.1", {"start": v(-21.62, 36.57) * mm, "end": v(-22.2, 38.44) * mm});
            skLineSegment(sketch, "E59.5.2", {"start": v(-22.2, 38.44) * mm, "end": v(-20.84, 37.02) * mm});
            skLineSegment(sketch, "E59.5.3", {"start": v(-20.84, 37.02) * mm, "end": v(-19.17, 34.13) * mm});
            skLineSegment(sketch, "E59.5.4", {"start": v(-19.17, 34.13) * mm, "end": v(-19.95, 33.68) * mm});
            skLineSegment(sketch, "E59.6.0", {"start": v(-27.99, 27.37) * mm, "end": v(-30.35, 29.73) * mm});
            skLineSegment(sketch, "E59.6.1", {"start": v(-30.35, 29.73) * mm, "end": v(-31.39, 31.39) * mm});
            skLineSegment(sketch, "E59.6.2", {"start": v(-31.39, 31.39) * mm, "end": v(-29.71, 30.36) * mm});
            skLineSegment(sketch, "E59.6.3", {"start": v(-29.71, 30.36) * mm, "end": v(-27.35, 28) * mm});
            skLineSegment(sketch, "E59.6.4", {"start": v(-27.35, 28) * mm, "end": v(-27.99, 27.37) * mm});
            skLineSegment(sketch, "E59.7.0", {"start": v(-34.12, 19.2) * mm, "end": v(-37, 20.86) * mm});
            skLineSegment(sketch, "E59.7.1", {"start": v(-37, 20.86) * mm, "end": v(-38.44, 22.2) * mm});
            skLineSegment(sketch, "E59.7.2", {"start": v(-38.44, 22.2) * mm, "end": v(-36.56, 21.64) * mm});
            skLineSegment(sketch, "E59.7.3", {"start": v(-36.56, 21.64) * mm, "end": v(-33.67, 19.97) * mm});
            skLineSegment(sketch, "E59.7.4", {"start": v(-33.67, 19.97) * mm, "end": v(-34.12, 19.2) * mm});
            skLineSegment(sketch, "E59.8.0", {"start": v(-37.92, 9.7) * mm, "end": v(-41.15, 10.57) * mm});
            skLineSegment(sketch, "E59.8.1", {"start": v(-41.15, 10.57) * mm, "end": v(-42.88, 11.49) * mm});
            skLineSegment(sketch, "E59.8.2", {"start": v(-42.88, 11.49) * mm, "end": v(-40.91, 11.44) * mm});
            skLineSegment(sketch, "E59.8.3", {"start": v(-40.91, 11.44) * mm, "end": v(-37.7, 10.57) * mm});
            skLineSegment(sketch, "E59.8.4", {"start": v(-37.7, 10.57) * mm, "end": v(-37.92, 9.7) * mm});
            skLineSegment(sketch, "E59.9.0", {"start": v(-39.14, -0.44) * mm, "end": v(-42.48, -0.44) * mm});
            skLineSegment(sketch, "E59.9.1", {"start": v(-42.48, -0.44) * mm, "end": v(-44.4, 0) * mm});
            skLineSegment(sketch, "E59.9.2", {"start": v(-44.4, 0) * mm, "end": v(-42.48, 0.46) * mm});
            skLineSegment(sketch, "E59.9.3", {"start": v(-42.48, 0.46) * mm, "end": v(-39.14, 0.46) * mm});
            skLineSegment(sketch, "E59.9.4", {"start": v(-39.14, 0.46) * mm, "end": v(-39.14, -0.44) * mm});
            skLineSegment(sketch, "E59.10.0", {"start": v(-37.7, -10.55) * mm, "end": v(-40.92, -11.42) * mm});
            skLineSegment(sketch, "E59.10.1", {"start": v(-40.92, -11.42) * mm, "end": v(-42.88, -11.49) * mm});
            skLineSegment(sketch, "E59.10.2", {"start": v(-42.88, -11.49) * mm, "end": v(-41.15, -10.55) * mm});
            skLineSegment(sketch, "E59.10.3", {"start": v(-41.15, -10.55) * mm, "end": v(-37.93, -9.69) * mm});
            skLineSegment(sketch, "E59.10.4", {"start": v(-37.93, -9.69) * mm, "end": v(-37.7, -10.55) * mm});
            skLineSegment(sketch, "E59.11.0", {"start": v(-33.68, -19.95) * mm, "end": v(-36.57, -21.62) * mm});
            skLineSegment(sketch, "E59.11.1", {"start": v(-36.57, -21.62) * mm, "end": v(-38.44, -22.2) * mm});
            skLineSegment(sketch, "E59.11.2", {"start": v(-38.44, -22.2) * mm, "end": v(-37.02, -20.84) * mm});
            skLineSegment(sketch, "E59.11.3", {"start": v(-37.02, -20.84) * mm, "end": v(-34.13, -19.17) * mm});
            skLineSegment(sketch, "E59.11.4", {"start": v(-34.13, -19.17) * mm, "end": v(-33.68, -19.95) * mm});
            skLineSegment(sketch, "E59.12.0", {"start": v(-27.37, -27.99) * mm, "end": v(-29.73, -30.35) * mm});
            skLineSegment(sketch, "E59.12.1", {"start": v(-29.73, -30.35) * mm, "end": v(-31.39, -31.39) * mm});
            skLineSegment(sketch, "E59.12.2", {"start": v(-31.39, -31.39) * mm, "end": v(-30.36, -29.71) * mm});
            skLineSegment(sketch, "E59.12.3", {"start": v(-30.36, -29.71) * mm, "end": v(-28, -27.35) * mm});
            skLineSegment(sketch, "E59.12.4", {"start": v(-28, -27.35) * mm, "end": v(-27.37, -27.99) * mm});
            skLineSegment(sketch, "E59.13.0", {"start": v(-19.2, -34.12) * mm, "end": v(-20.86, -37) * mm});
            skLineSegment(sketch, "E59.13.1", {"start": v(-20.86, -37) * mm, "end": v(-22.2, -38.44) * mm});
            skLineSegment(sketch, "E59.13.2", {"start": v(-22.2, -38.44) * mm, "end": v(-21.64, -36.56) * mm});
            skLineSegment(sketch, "E59.13.3", {"start": v(-21.64, -36.56) * mm, "end": v(-19.97, -33.67) * mm});
            skLineSegment(sketch, "E59.13.4", {"start": v(-19.97, -33.67) * mm, "end": v(-19.2, -34.12) * mm});
            skLineSegment(sketch, "E59.14.0", {"start": v(-9.7, -37.92) * mm, "end": v(-10.57, -41.15) * mm});
            skLineSegment(sketch, "E59.14.1", {"start": v(-10.57, -41.15) * mm, "end": v(-11.49, -42.88) * mm});
            skLineSegment(sketch, "E59.14.2", {"start": v(-11.49, -42.88) * mm, "end": v(-11.44, -40.91) * mm});
            skLineSegment(sketch, "E59.14.3", {"start": v(-11.44, -40.91) * mm, "end": v(-10.57, -37.7) * mm});
            skLineSegment(sketch, "E59.14.4", {"start": v(-10.57, -37.7) * mm, "end": v(-9.7, -37.92) * mm});
            skLineSegment(sketch, "E59.15.0", {"start": v(0.44, -39.14) * mm, "end": v(0.44, -42.48) * mm});
            skLineSegment(sketch, "E59.15.1", {"start": v(0.44, -42.48) * mm, "end": v(0, -44.4) * mm});
            skLineSegment(sketch, "E59.15.2", {"start": v(0, -44.4) * mm, "end": v(-0.46, -42.48) * mm});
            skLineSegment(sketch, "E59.15.3", {"start": v(-0.46, -42.48) * mm, "end": v(-0.46, -39.14) * mm});
            skLineSegment(sketch, "E59.15.4", {"start": v(-0.46, -39.14) * mm, "end": v(0.44, -39.14) * mm});
            skLineSegment(sketch, "E59.16.0", {"start": v(10.55, -37.7) * mm, "end": v(11.42, -40.92) * mm});
            skLineSegment(sketch, "E59.16.1", {"start": v(11.42, -40.92) * mm, "end": v(11.49, -42.88) * mm});
            skLineSegment(sketch, "E59.16.2", {"start": v(11.49, -42.88) * mm, "end": v(10.55, -41.15) * mm});
            skLineSegment(sketch, "E59.16.3", {"start": v(10.55, -41.15) * mm, "end": v(9.69, -37.93) * mm});
            skLineSegment(sketch, "E59.16.4", {"start": v(9.69, -37.93) * mm, "end": v(10.55, -37.7) * mm});
            skLineSegment(sketch, "E59.17.0", {"start": v(19.95, -33.68) * mm, "end": v(21.62, -36.57) * mm});
            skLineSegment(sketch, "E59.17.1", {"start": v(21.62, -36.57) * mm, "end": v(22.2, -38.44) * mm});
            skLineSegment(sketch, "E59.17.2", {"start": v(22.2, -38.44) * mm, "end": v(20.84, -37.02) * mm});
            skLineSegment(sketch, "E59.17.3", {"start": v(20.84, -37.02) * mm, "end": v(19.17, -34.13) * mm});
            skLineSegment(sketch, "E59.17.4", {"start": v(19.17, -34.13) * mm, "end": v(19.95, -33.68) * mm});
            skLineSegment(sketch, "E59.18.0", {"start": v(27.99, -27.37) * mm, "end": v(30.35, -29.73) * mm});
            skLineSegment(sketch, "E59.18.1", {"start": v(30.35, -29.73) * mm, "end": v(31.39, -31.39) * mm});
            skLineSegment(sketch, "E59.18.2", {"start": v(31.39, -31.39) * mm, "end": v(29.71, -30.36) * mm});
            skLineSegment(sketch, "E59.18.3", {"start": v(29.71, -30.36) * mm, "end": v(27.35, -28) * mm});
            skLineSegment(sketch, "E59.18.4", {"start": v(27.35, -28) * mm, "end": v(27.99, -27.37) * mm});
            skLineSegment(sketch, "E59.19.0", {"start": v(34.12, -19.2) * mm, "end": v(37, -20.86) * mm});
            skLineSegment(sketch, "E59.19.1", {"start": v(37, -20.86) * mm, "end": v(38.44, -22.2) * mm});
            skLineSegment(sketch, "E59.19.2", {"start": v(38.44, -22.2) * mm, "end": v(36.56, -21.64) * mm});
            skLineSegment(sketch, "E59.19.3", {"start": v(36.56, -21.64) * mm, "end": v(33.67, -19.97) * mm});
            skLineSegment(sketch, "E59.19.4", {"start": v(33.67, -19.97) * mm, "end": v(34.12, -19.2) * mm});
            skLineSegment(sketch, "E59.20.0", {"start": v(37.92, -9.7) * mm, "end": v(41.15, -10.57) * mm});
            skLineSegment(sketch, "E59.20.1", {"start": v(41.15, -10.57) * mm, "end": v(42.88, -11.49) * mm});
            skLineSegment(sketch, "E59.20.2", {"start": v(42.88, -11.49) * mm, "end": v(40.91, -11.44) * mm});
            skLineSegment(sketch, "E59.20.3", {"start": v(40.91, -11.44) * mm, "end": v(37.7, -10.57) * mm});
            skLineSegment(sketch, "E59.20.4", {"start": v(37.7, -10.57) * mm, "end": v(37.92, -9.7) * mm});
            skLineSegment(sketch, "E59.21.0", {"start": v(39.14, 0.44) * mm, "end": v(42.48, 0.44) * mm});
            skLineSegment(sketch, "E59.21.1", {"start": v(42.48, 0.44) * mm, "end": v(44.4, 0) * mm});
            skLineSegment(sketch, "E59.21.2", {"start": v(44.4, 0) * mm, "end": v(42.48, -0.46) * mm});
            skLineSegment(sketch, "E59.21.3", {"start": v(42.48, -0.46) * mm, "end": v(39.14, -0.46) * mm});
            skLineSegment(sketch, "E59.21.4", {"start": v(39.14, -0.46) * mm, "end": v(39.14, 0.44) * mm});
            skLineSegment(sketch, "E59.22.0", {"start": v(37.7, 10.55) * mm, "end": v(40.92, 11.42) * mm});
            skLineSegment(sketch, "E59.22.1", {"start": v(40.92, 11.42) * mm, "end": v(42.88, 11.49) * mm});
            skLineSegment(sketch, "E59.22.2", {"start": v(42.88, 11.49) * mm, "end": v(41.15, 10.55) * mm});
            skLineSegment(sketch, "E59.22.3", {"start": v(41.15, 10.55) * mm, "end": v(37.93, 9.69) * mm});
            skLineSegment(sketch, "E59.22.4", {"start": v(37.93, 9.69) * mm, "end": v(37.7, 10.55) * mm});
            skLineSegment(sketch, "E59.23.0", {"start": v(33.68, 19.95) * mm, "end": v(36.57, 21.62) * mm});
            skLineSegment(sketch, "E59.23.1", {"start": v(36.57, 21.62) * mm, "end": v(38.44, 22.2) * mm});
            skLineSegment(sketch, "E59.23.2", {"start": v(38.44, 22.2) * mm, "end": v(37.02, 20.84) * mm});
            skLineSegment(sketch, "E59.23.3", {"start": v(37.02, 20.84) * mm, "end": v(34.13, 19.17) * mm});
            skLineSegment(sketch, "E59.23.4", {"start": v(34.13, 19.17) * mm, "end": v(33.68, 19.95) * mm});
            skPoint(sketch, "E59.center", {"position": v(0, 0) * mm});
            skText(sketch, "E60", { "text": "135", "fontName": "OpenSans-Bold.ttf"});
            skText(sketch, "E61", { "text": "225", "fontName": "OpenSans-Bold.ttf"});
            skText(sketch, "E62", { "text": "315", "fontName": "OpenSans-Bold.ttf"});
            skLineSegment(sketch, "E63", {"start": v(29.48, 22.68) * mm, "end": v(-26.7, 22.68) * mm, "construction": true});
            const initialGuessF5  = {"E58": [0.02268, 0.02268, 1, 0, 0.00421], "E60": [0.02124, -0.02737, 1, 0, 0.00422], "E61": [-0.02942, -0.02703, 1, 0, 0.00431], "E62": [-0.02818, 0.02271, 1, 0, 0.004]};
            skSetInitialGuess(sketch, initialGuessF5);
            skSolve(sketch);
        }
        {
            var Q0;
            Q0 = qSketchRegion(id + "F5", true);
            extrude(context, id + "F6", {"entities" : qUnion([Q0]), "operationType" : NewBodyOperationType.ADD, "depth" : 1 * mm});
        }
        {
            var Q0;
            {var subQ0=sQuery(id+"F0.wireOp",EDGE,"E28.40.0");var subQ2=sQuery(id+"F0.wireOp",EDGE,"E28.39.0");var subQ4=sQuery(id+"F0.wireOp",EDGE,"E28.38.0");var subQ6=sQuery(id+"F0.wireOp",EDGE,"E28.35.0");var subQ8=sQuery(id+"F0.wireOp",EDGE,"E28.34.0");var subQ10=sQuery(id+"F0.wireOp",EDGE,"E28.33.0");var subQ12=sQuery(id+"F0.wireOp",EDGE,"E28.25.0");var subQ14=sQuery(id+"F0.wireOp",EDGE,"E28.24.0");var subQ16=sQuery(id+"F0.wireOp",EDGE,"E28.16.0");var subQ18=sQuery(id+"F0.wireOp",EDGE,"E24");var subQ20=sQuery(id+"F0.wireOp",EDGE,"E23");var subQ22=sQuery(id+"F0.wireOp",EDGE,"E21");var subQ23=makeQuery(id+"F1.opExtrude","SWEPT_FACE",FACE,{"disambiguationData":[OSD([subQ22])]});var subQ24=sQuery(id+"F0.wireOp",EDGE,"E22");var subQ25=sQuery(id+"F0.wireOp",EDGE,"E3");var subQ26=sQuery(id+"F0.wireOp",EDGE,"E25.1.2");var subQ28=sQuery(id+"F0.wireOp",EDGE,"E25.3.0");var subQ38=sQuery(id+"F0.wireOp",EDGE,"E28.32.0");var subQ41=sQuery(id+"F0.wireOp",EDGE,"E28.31.0");var subQ44=sQuery(id+"F0.wireOp",EDGE,"E28.30.0");var subQ47=sQuery(id+"F0.wireOp",EDGE,"E28.29.0");var subQ50=sQuery(id+"F0.wireOp",EDGE,"E28.28.0");var subQ53=sQuery(id+"F0.wireOp",EDGE,"E28.27.0");var subQ56=sQuery(id+"F0.wireOp",EDGE,"E28.26.0");var subQ59=sQuery(id+"F0.wireOp",EDGE,"E28.23.0");var subQ62=sQuery(id+"F0.wireOp",EDGE,"E28.22.0");var subQ65=sQuery(id+"F0.wireOp",EDGE,"E28.21.0");var subQ68=sQuery(id+"F0.wireOp",EDGE,"E28.20.0");var subQ71=sQuery(id+"F0.wireOp",EDGE,"E28.19.0");var subQ74=sQuery(id+"F0.wireOp",EDGE,"E28.18.0");var subQ77=sQuery(id+"F0.wireOp",EDGE,"E28.17.0");var subQ81=sQuery(id+"F0.wireOp",EDGE,"E28.13.0");var subQ84=sQuery(id+"F0.wireOp",EDGE,"E28.12.0");var subQ87=sQuery(id+"F0.wireOp",EDGE,"E28.11.0");var subQ90=sQuery(id+"F0.wireOp",EDGE,"E28.71.0");var subQ93=sQuery(id+"F0.wireOp",EDGE,"E28.70.0");var subQ101=sQuery(id+"F0.wireOp",EDGE,"E28.64.0");var subQ104=sQuery(id+"F0.wireOp",EDGE,"E28.63.0");var subQ112=sQuery(id+"F0.wireOp",EDGE,"E28.57.0");var subQ115=sQuery(id+"F0.wireOp",EDGE,"E28.56.0");var subQ117=sQuery(id+"F0.wireOp",EDGE,"E28.54.0");var subQ120=sQuery(id+"F0.wireOp",EDGE,"E28.53.0");var subQ123=sQuery(id+"F0.wireOp",EDGE,"E28.52.0");var subQ126=sQuery(id+"F0.wireOp",EDGE,"E28.51.0");var subQ129=sQuery(id+"F0.wireOp",EDGE,"E28.50.0");var subQ132=sQuery(id+"F0.wireOp",EDGE,"E28.49.0");var subQ134=sQuery(id+"F0.wireOp",EDGE,"E28.48.0");var subQ136=sQuery(id+"F0.wireOp",EDGE,"E28.47.0");var subQ138=sQuery(id+"F0.wireOp",EDGE,"E28.69.0");var subQ141=sQuery(id+"F0.wireOp",EDGE,"E28.68.0");var subQ144=sQuery(id+"F0.wireOp",EDGE,"E28.67.0");var subQ147=sQuery(id+"F0.wireOp",EDGE,"E28.66.0");var subQ150=sQuery(id+"F0.wireOp",EDGE,"E28.65.0");var subQ153=sQuery(id+"F0.wireOp",EDGE,"E28.62.0");var subQ156=sQuery(id+"F0.wireOp",EDGE,"E28.61.0");var subQ159=sQuery(id+"F0.wireOp",EDGE,"E28.60.0");var subQ162=sQuery(id+"F0.wireOp",EDGE,"E28.59.0");var subQ165=sQuery(id+"F0.wireOp",EDGE,"E28.58.0");var subQ168=sQuery(id+"F0.wireOp",EDGE,"E28.55.0");var subQ173=sQuery(id+"F0.wireOp",EDGE,"E28.3.0");var subQ177=sQuery(id+"F0.wireOp",EDGE,"E28.2.0");var subQ179=sQuery(id+"F0.wireOp",EDGE,"E28.1.0");var subQ181=sQuery(id+"F0.wireOp",EDGE,"E27");var subQ185=sQuery(id+"F0.wireOp",EDGE,"E28.8.0");var subQ187=sQuery(id+"F0.wireOp",EDGE,"E25.3.2");var subQ189=sQuery(id+"F0.wireOp",EDGE,"E25.3.1");var subQ192=sQuery(id+"F0.wireOp",EDGE,"E25.2.2");var subQ195=sQuery(id+"F0.wireOp",EDGE,"E25.2.1");var subQ198=sQuery(id+"F0.wireOp",EDGE,"E25.2.0");var subQ202=sQuery(id+"F0.wireOp",EDGE,"E25.1.0");var subQ204=sQuery(id+"F0.wireOp",EDGE,"E28.9.0");var subQ210=sQuery(id+"F0.wireOp",EDGE,"E28.10.0");var subQ216=sQuery(id+"F0.wireOp",EDGE,"E28.4.0");var subQ218=sQuery(id+"F0.wireOp",EDGE,"E28.5.0");var subQ222=sQuery(id+"F0.wireOp",EDGE,"E25.1.1");var subQ229=sQuery(id+"F0.wireOp",EDGE,"E28.36.0");var subQ233=sQuery(id+"F0.wireOp",EDGE,"E28.14.0");var subQ235=sQuery(id+"F0.wireOp",EDGE,"E28.37.0");var subQ239=sQuery(id+"F0.wireOp",EDGE,"E28.15.0");var subQ241=sQuery(id+"F0.wireOp",EDGE,"E28.6.0");var subQ244=sQuery(id+"F0.wireOp",EDGE,"E28.7.0");var subQ249=sQuery(id+"F0.wireOp",EDGE,"E28.41.0");var subQ253=sQuery(id+"F0.wireOp",EDGE,"E28.42.0");var subQ256=sQuery(id+"F0.wireOp",EDGE,"E28.43.0");var subQ259=sQuery(id+"F0.wireOp",EDGE,"E28.44.0");var subQ262=sQuery(id+"F0.wireOp",EDGE,"E28.45.0");var subQ265=sQuery(id+"F0.wireOp",EDGE,"E28.46.0");Q0=makeQuery(id+"F6.boolean.opBoolean","SPLIT",FACE,{"disambiguationData":[TD([subQ23])],"derivedFrom":makeQuery(id+"F4.boolean.opBoolean","SPLIT",FACE,{"disambiguationData":[TD([subQ23])],"derivedFrom":makeQuery(id+"F1.opExtrude","CAP_FACE",FACE,{"disambiguationData":[OSD([subQ25,subQ22,subQ24,subQ20,subQ18,subQ202,subQ222,subQ26,subQ198,subQ195,subQ192,subQ28,subQ189,subQ187,subQ181,subQ179,subQ177,subQ173,subQ216,subQ218,subQ241,subQ244,subQ185,subQ204,subQ210,subQ87,subQ84,subQ81,subQ233,subQ239,subQ16,subQ77,subQ74,subQ71,subQ68,subQ65,subQ62,subQ59,subQ14,subQ12,subQ56,subQ53,subQ50,subQ47,subQ44,subQ41,subQ38,subQ10,subQ8,subQ6,subQ229,subQ235,subQ4,subQ2,subQ0,subQ249,subQ253,subQ256,subQ259,subQ262,subQ265,subQ136,subQ134,subQ132,subQ129,subQ126,subQ123,subQ120,subQ117,subQ168,subQ115,subQ112,subQ165,subQ162,subQ159,subQ156,subQ153,subQ104,subQ101,subQ150,subQ147,subQ144,subQ141,subQ138,subQ93,subQ90])],"isStart":false})})});}
            var sketch = newSketch(context, id + "F7", { "sketchPlane" : qUnion([Q0])});
            skCircle(sketch, "E64", {"center": v(0, 0) * mm, "radius": 38.32 * mm});
            skCircle(sketch, "E65", {"center": v(0, 0) * mm, "radius": 25.06 * mm});
            skLineSegment(sketch, "E66", {"start": v(-9.4, 37.14) * mm, "end": v(-7.1, 24.03) * mm});
            skLineSegment(sketch, "E67", {"start": v(7.19, 24) * mm, "end": v(9.5, 37.12) * mm});
            skLineSegment(sketch, "E68", {"start": v(23.98, 7.27) * mm, "end": v(37.1, 9.58) * mm});
            skLineSegment(sketch, "E69", {"start": v(24.65, -4.5) * mm, "end": v(37.11, -9.53) * mm});
            skLineSegment(sketch, "E70", {"start": v(-24.03, 7.11) * mm, "end": v(-37.14, 9.42) * mm});
            skLineSegment(sketch, "E71", {"start": v(-24.66, -4.46) * mm, "end": v(-37.12, -9.5) * mm});
            skLineSegment(sketch, "E72", {"start": v(-8.38, -23.61) * mm, "end": v(-10.7, -36.8) * mm});
            skLineSegment(sketch, "E73", {"start": v(9.1, -23.35) * mm, "end": v(11.42, -36.57) * mm});
            skLineSegment(sketch, "E74", {"start": v(-19.51, 32.98) * mm, "end": v(-13.87, 20.87) * mm});
            skLineSegment(sketch, "E75", {"start": v(-32.78, 19.83) * mm, "end": v(-20.66, 14.18) * mm});
            skLineSegment(sketch, "E76", {"start": v(14.18, 20.66) * mm, "end": v(19.84, 32.78) * mm});
            skLineSegment(sketch, "E77", {"start": v(20.91, 13.8) * mm, "end": v(33.01, 19.45) * mm});
            skLineSegment(sketch, "E78", {"start": v(13.93, -20.83) * mm, "end": v(19.58, -32.94) * mm});
            skLineSegment(sketch, "E79", {"start": v(20.92, -13.79) * mm, "end": v(33.02, -19.43) * mm});
            skLineSegment(sketch, "E80", {"start": v(-20.83, -13.92) * mm, "end": v(-32.94, -19.57) * mm});
            skLineSegment(sketch, "E81", {"start": v(-13.92, -20.84) * mm, "end": v(-19.57, -32.94) * mm});
            skLineSegment(sketch, "E82", {"start": v(-9.04, 0) * mm, "end": v(11.2, 0) * mm, "construction": true});
            skLineSegment(sketch, "E83", {"start": v(0, 7.83) * mm, "end": v(0, -6.14) * mm, "construction": true});
            skSolve(sketch);
        }
        {
            var Q0;
            {var subQ0=sQuery(id+"F7.wireOp",EDGE,"E66");Q0=makeQuery(id+"F7.imprint","IMPRINT",FACE,{"disambiguationData":[TD([[makeQuery(id+"F7.imprint","IMPRINT",EDGE,{"derivedFrom":subQ0}),-1.0]])]});}
            var Q1;
            {var subQ0=sQuery(id+"F7.wireOp",EDGE,"E67");Q1=makeQuery(id+"F7.imprint","IMPRINT",FACE,{"disambiguationData":[TD([[makeQuery(id+"F7.imprint","IMPRINT",EDGE,{"derivedFrom":subQ0}),-1.0]])]});}
            var Q2;
            {var subQ0=sQuery(id+"F7.wireOp",EDGE,"E68");Q2=makeQuery(id+"F7.imprint","IMPRINT",FACE,{"disambiguationData":[TD([[makeQuery(id+"F7.imprint","IMPRINT",EDGE,{"derivedFrom":subQ0}),1.0]])]});}
            var Q3;
            {var subQ0=sQuery(id+"F7.wireOp",EDGE,"E69");Q3=makeQuery(id+"F7.imprint","IMPRINT",FACE,{"disambiguationData":[TD([[makeQuery(id+"F7.imprint","IMPRINT",EDGE,{"derivedFrom":subQ0}),-1.0]])]});}
            var Q4;
            {var subQ0=sQuery(id+"F7.wireOp",EDGE,"E73");Q4=makeQuery(id+"F7.imprint","IMPRINT",FACE,{"disambiguationData":[TD([[makeQuery(id+"F7.imprint","IMPRINT",EDGE,{"derivedFrom":subQ0}),1.0]])]});}
            var Q5;
            {var subQ0=sQuery(id+"F7.wireOp",EDGE,"E72");Q5=makeQuery(id+"F7.imprint","IMPRINT",FACE,{"disambiguationData":[TD([[makeQuery(id+"F7.imprint","IMPRINT",EDGE,{"derivedFrom":subQ0}),-1.0]])]});}
            var Q6;
            {var subQ0=sQuery(id+"F7.wireOp",EDGE,"E71");Q6=makeQuery(id+"F7.imprint","IMPRINT",FACE,{"disambiguationData":[TD([[makeQuery(id+"F7.imprint","IMPRINT",EDGE,{"derivedFrom":subQ0}),1.0]])]});}
            var Q7;
            {var subQ0=sQuery(id+"F7.wireOp",EDGE,"E70");Q7=makeQuery(id+"F7.imprint","IMPRINT",FACE,{"disambiguationData":[TD([[makeQuery(id+"F7.imprint","IMPRINT",EDGE,{"derivedFrom":subQ0}),-1.0]])]});}
            extrude(context, id + "F8", {"entities" : qUnion([Q0, Q1, Q2, Q3, Q4, Q5, Q6, Q7]), "operationType" : NewBodyOperationType.REMOVE, "endBound" : BoundingType.THROUGH_ALL, "oppositeDirection" : true, "depth" : 25 * mm});
        }
        {
            var Q0;
            Q0=makeQuery(id+"F8.boolean.opBoolean","COPY",EDGE,{"derivedFrom":makeQuery(id+"F8.opExtrude","SWEPT_EDGE",EDGE,{"disambiguationData":[OSD([sQuery(id+"F7.wireOp",EDGE,"E65"),sQuery(id+"F7.wireOp",EDGE,"E74")])]})});
            var Q1;
            Q1=makeQuery(id+"F8.boolean.opBoolean","COPY",EDGE,{"derivedFrom":makeQuery(id+"F8.opExtrude","SWEPT_EDGE",EDGE,{"disambiguationData":[OSD([sQuery(id+"F7.wireOp",EDGE,"E65"),sQuery(id+"F7.wireOp",EDGE,"E66")])]})});
            var Q2;
            Q2=makeQuery(id+"F8.boolean.opBoolean","COPY",EDGE,{"derivedFrom":makeQuery(id+"F8.opExtrude","SWEPT_EDGE",EDGE,{"disambiguationData":[OSD([sQuery(id+"F7.wireOp",EDGE,"E64"),sQuery(id+"F7.wireOp",EDGE,"E74")])]})});
            var Q3;
            Q3=makeQuery(id+"F8.boolean.opBoolean","COPY",EDGE,{"derivedFrom":makeQuery(id+"F8.opExtrude","SWEPT_EDGE",EDGE,{"disambiguationData":[OSD([sQuery(id+"F7.wireOp",EDGE,"E64"),sQuery(id+"F7.wireOp",EDGE,"E66")])]})});
            var Q4;
            Q4=makeQuery(id+"F8.boolean.opBoolean","COPY",EDGE,{"derivedFrom":makeQuery(id+"F8.opExtrude","SWEPT_EDGE",EDGE,{"disambiguationData":[OSD([sQuery(id+"F7.wireOp",EDGE,"E64"),sQuery(id+"F7.wireOp",EDGE,"E67")])]})});
            var Q5;
            Q5=makeQuery(id+"F8.boolean.opBoolean","COPY",EDGE,{"derivedFrom":makeQuery(id+"F8.opExtrude","SWEPT_EDGE",EDGE,{"disambiguationData":[OSD([sQuery(id+"F7.wireOp",EDGE,"E64"),sQuery(id+"F7.wireOp",EDGE,"E76")])]})});
            var Q6;
            Q6=makeQuery(id+"F8.boolean.opBoolean","COPY",EDGE,{"derivedFrom":makeQuery(id+"F8.opExtrude","SWEPT_EDGE",EDGE,{"disambiguationData":[OSD([sQuery(id+"F7.wireOp",EDGE,"E65"),sQuery(id+"F7.wireOp",EDGE,"E67")])]})});
            var Q7;
            Q7=makeQuery(id+"F8.boolean.opBoolean","COPY",EDGE,{"derivedFrom":makeQuery(id+"F8.opExtrude","SWEPT_EDGE",EDGE,{"disambiguationData":[OSD([sQuery(id+"F7.wireOp",EDGE,"E65"),sQuery(id+"F7.wireOp",EDGE,"E76")])]})});
            var Q8;
            Q8=makeQuery(id+"F8.boolean.opBoolean","COPY",EDGE,{"derivedFrom":makeQuery(id+"F8.opExtrude","SWEPT_EDGE",EDGE,{"disambiguationData":[OSD([sQuery(id+"F7.wireOp",EDGE,"E65"),sQuery(id+"F7.wireOp",EDGE,"E77")])]})});
            var Q9;
            Q9=makeQuery(id+"F8.boolean.opBoolean","COPY",EDGE,{"derivedFrom":makeQuery(id+"F8.opExtrude","SWEPT_EDGE",EDGE,{"disambiguationData":[OSD([sQuery(id+"F7.wireOp",EDGE,"E64"),sQuery(id+"F7.wireOp",EDGE,"E68")])]})});
            var Q10;
            Q10=makeQuery(id+"F8.boolean.opBoolean","COPY",EDGE,{"derivedFrom":makeQuery(id+"F8.opExtrude","SWEPT_EDGE",EDGE,{"disambiguationData":[OSD([sQuery(id+"F7.wireOp",EDGE,"E64"),sQuery(id+"F7.wireOp",EDGE,"E77")])]})});
            var Q11;
            Q11=makeQuery(id+"F8.boolean.opBoolean","COPY",EDGE,{"derivedFrom":makeQuery(id+"F8.opExtrude","SWEPT_EDGE",EDGE,{"disambiguationData":[OSD([sQuery(id+"F7.wireOp",EDGE,"E65"),sQuery(id+"F7.wireOp",EDGE,"E68")])]})});
            var Q12;
            Q12=makeQuery(id+"F8.boolean.opBoolean","COPY",EDGE,{"derivedFrom":makeQuery(id+"F8.opExtrude","SWEPT_EDGE",EDGE,{"disambiguationData":[OSD([sQuery(id+"F7.wireOp",EDGE,"E65"),sQuery(id+"F7.wireOp",EDGE,"E69")])]})});
            var Q13;
            Q13=makeQuery(id+"F8.boolean.opBoolean","COPY",EDGE,{"derivedFrom":makeQuery(id+"F8.opExtrude","SWEPT_EDGE",EDGE,{"disambiguationData":[OSD([sQuery(id+"F7.wireOp",EDGE,"E64"),sQuery(id+"F7.wireOp",EDGE,"E69")])]})});
            var Q14;
            Q14=makeQuery(id+"F8.boolean.opBoolean","COPY",EDGE,{"derivedFrom":makeQuery(id+"F8.opExtrude","SWEPT_EDGE",EDGE,{"disambiguationData":[OSD([sQuery(id+"F7.wireOp",EDGE,"E65"),sQuery(id+"F7.wireOp",EDGE,"E79")])]})});
            var Q15;
            Q15=makeQuery(id+"F8.boolean.opBoolean","COPY",EDGE,{"derivedFrom":makeQuery(id+"F8.opExtrude","SWEPT_EDGE",EDGE,{"disambiguationData":[OSD([sQuery(id+"F7.wireOp",EDGE,"E64"),sQuery(id+"F7.wireOp",EDGE,"E79")])]})});
            var Q16;
            Q16=makeQuery(id+"F8.boolean.opBoolean","COPY",EDGE,{"derivedFrom":makeQuery(id+"F8.opExtrude","SWEPT_EDGE",EDGE,{"disambiguationData":[OSD([sQuery(id+"F7.wireOp",EDGE,"E65"),sQuery(id+"F7.wireOp",EDGE,"E78")])]})});
            var Q17;
            Q17=makeQuery(id+"F8.boolean.opBoolean","COPY",EDGE,{"derivedFrom":makeQuery(id+"F8.opExtrude","SWEPT_EDGE",EDGE,{"disambiguationData":[OSD([sQuery(id+"F7.wireOp",EDGE,"E65"),sQuery(id+"F7.wireOp",EDGE,"E73")])]})});
            var Q18;
            Q18=makeQuery(id+"F8.boolean.opBoolean","COPY",EDGE,{"derivedFrom":makeQuery(id+"F8.opExtrude","SWEPT_EDGE",EDGE,{"disambiguationData":[OSD([sQuery(id+"F7.wireOp",EDGE,"E64"),sQuery(id+"F7.wireOp",EDGE,"E78")])]})});
            var Q19;
            Q19=makeQuery(id+"F8.boolean.opBoolean","COPY",EDGE,{"derivedFrom":makeQuery(id+"F8.opExtrude","SWEPT_EDGE",EDGE,{"disambiguationData":[OSD([sQuery(id+"F7.wireOp",EDGE,"E64"),sQuery(id+"F7.wireOp",EDGE,"E73")])]})});
            var Q20;
            Q20=makeQuery(id+"F8.boolean.opBoolean","COPY",EDGE,{"derivedFrom":makeQuery(id+"F8.opExtrude","SWEPT_EDGE",EDGE,{"disambiguationData":[OSD([sQuery(id+"F7.wireOp",EDGE,"E64"),sQuery(id+"F7.wireOp",EDGE,"E81")])]})});
            var Q21;
            Q21=makeQuery(id+"F8.boolean.opBoolean","COPY",EDGE,{"derivedFrom":makeQuery(id+"F8.opExtrude","SWEPT_EDGE",EDGE,{"disambiguationData":[OSD([sQuery(id+"F7.wireOp",EDGE,"E65"),sQuery(id+"F7.wireOp",EDGE,"E81")])]})});
            var Q22;
            Q22=makeQuery(id+"F8.boolean.opBoolean","COPY",EDGE,{"derivedFrom":makeQuery(id+"F8.opExtrude","SWEPT_EDGE",EDGE,{"disambiguationData":[OSD([sQuery(id+"F7.wireOp",EDGE,"E65"),sQuery(id+"F7.wireOp",EDGE,"E72")])]})});
            var Q23;
            Q23=makeQuery(id+"F8.boolean.opBoolean","COPY",EDGE,{"derivedFrom":makeQuery(id+"F8.opExtrude","SWEPT_EDGE",EDGE,{"disambiguationData":[OSD([sQuery(id+"F7.wireOp",EDGE,"E64"),sQuery(id+"F7.wireOp",EDGE,"E72")])]})});
            var Q24;
            Q24=makeQuery(id+"F8.boolean.opBoolean","COPY",EDGE,{"derivedFrom":makeQuery(id+"F8.opExtrude","SWEPT_EDGE",EDGE,{"disambiguationData":[OSD([sQuery(id+"F7.wireOp",EDGE,"E65"),sQuery(id+"F7.wireOp",EDGE,"E71")])]})});
            var Q25;
            Q25=makeQuery(id+"F8.boolean.opBoolean","COPY",EDGE,{"derivedFrom":makeQuery(id+"F8.opExtrude","SWEPT_EDGE",EDGE,{"disambiguationData":[OSD([sQuery(id+"F7.wireOp",EDGE,"E64"),sQuery(id+"F7.wireOp",EDGE,"E80")])]})});
            var Q26;
            Q26=makeQuery(id+"F8.boolean.opBoolean","COPY",EDGE,{"derivedFrom":makeQuery(id+"F8.opExtrude","SWEPT_EDGE",EDGE,{"disambiguationData":[OSD([sQuery(id+"F7.wireOp",EDGE,"E65"),sQuery(id+"F7.wireOp",EDGE,"E80")])]})});
            var Q27;
            Q27=makeQuery(id+"F8.boolean.opBoolean","COPY",EDGE,{"derivedFrom":makeQuery(id+"F8.opExtrude","SWEPT_EDGE",EDGE,{"disambiguationData":[OSD([sQuery(id+"F7.wireOp",EDGE,"E64"),sQuery(id+"F7.wireOp",EDGE,"E71")])]})});
            var Q28;
            Q28=makeQuery(id+"F8.boolean.opBoolean","COPY",EDGE,{"derivedFrom":makeQuery(id+"F8.opExtrude","SWEPT_EDGE",EDGE,{"disambiguationData":[OSD([sQuery(id+"F7.wireOp",EDGE,"E65"),sQuery(id+"F7.wireOp",EDGE,"E70")])]})});
            var Q29;
            Q29=makeQuery(id+"F8.boolean.opBoolean","COPY",EDGE,{"derivedFrom":makeQuery(id+"F8.opExtrude","SWEPT_EDGE",EDGE,{"disambiguationData":[OSD([sQuery(id+"F7.wireOp",EDGE,"E64"),sQuery(id+"F7.wireOp",EDGE,"E70")])]})});
            var Q30;
            Q30=makeQuery(id+"F8.boolean.opBoolean","COPY",EDGE,{"derivedFrom":makeQuery(id+"F8.opExtrude","SWEPT_EDGE",EDGE,{"disambiguationData":[OSD([sQuery(id+"F7.wireOp",EDGE,"E64"),sQuery(id+"F7.wireOp",EDGE,"E75")])]})});
            var Q31;
            Q31=makeQuery(id+"F8.boolean.opBoolean","COPY",EDGE,{"derivedFrom":makeQuery(id+"F8.opExtrude","SWEPT_EDGE",EDGE,{"disambiguationData":[OSD([sQuery(id+"F7.wireOp",EDGE,"E65"),sQuery(id+"F7.wireOp",EDGE,"E75")])]})});
            fillet(context, id + "F9", {"entities" : qUnion([Q0, Q1, Q2, Q3, Q4, Q5, Q6, Q7, Q8, Q9, Q10, Q11, Q12, Q13, Q14, Q15, Q16, Q17, Q18, Q19, Q20, Q21, Q22, Q23, Q24, Q25, Q26, Q27, Q28, Q29, Q30, Q31]), "radius" : 2 * mm, "tangentPropagation" : true, "allowEdgeOverflow" : false});
        }
    });
